# Revit family: Reece_Basin_Alape_Scopio_Freestanding Basin_400 mm
name_source: partatom
category: Plumbing Fixtures
revit_build: Autodesk Revit 2018 (Build: 20180329_1100(x64)
units: mm (PartAtom-declared; Revit-internal decimal feet)

## family parameters
Always vertical = Yes
Cut with Voids When Loaded = Yes
Part Type = Normal
Room Calculation Point = Yes
Round Connector Dimension = Use Diameter
Shared = Yes
Work Plane-Based = Yes

## types (1)
- 8.7 L_Enamelled Glazed Steel_White
    Default Elevation = 0 mm  [stored 0 ft]
    Description = Alape Scopio Freestanding Basin 400mm White
    Disclaimer = THIS FILE IS THE PROPERTY OF THE REECE GROUP. IT MAY NOT BE REPRODUCED, REVERSE-ENGINEERED OR MODIFIED. ANY REPUBLICATION, TRANSMISSION OR DISTRIBUTION FOR THE PURPOSE OF COMMERCIALLY EXPLOITING THE FILES IS PROHIBITED.
    Keynote = Product #9508138, Reece_Basin_Alape_Scopio_Freestanding Basin_400 mm - 8.7 L_Enamelled Glazed Steel_White
    Manufacturer = Alape
    Model = Scopio
    Reece_Basin_Outlet = 32 mm  [stored 0.104987 ft]
    Reece_Detail_Additional = With Wall Connection
    Reece_Detail_Connector = No Taphole
    Reece_Detail_Disclaimer = THIS FILE IS THE PROPERTY OF THE REECE GROUP. IT MAY NOT BE REPRODUCED, REVERSE-ENGINEERED OR MODIFIED. ANY REPUBLICATION, TRANSMISSION OR DISTRIBUTION FOR THE PURPOSE OF COMMERCIALLY EXPLOITING THE FILES IS PROHIBITED.
    Reece_Detail_Installation = Freestanding Basin
    Reece_Material_Main = Reece_Metal_Steel Enamelled_White
    Reece_Overall_Capacity = 8.7 L
    Reece_Overall_Height = 900 mm  [stored 2.95276 ft]
    Reece_Overall_Length = 425 mm  [stored 1.39436 ft]
    Reece_Overall_Width = 400 mm  [stored 1.31234 ft]
    Reece_Product_Brand = Alape
    Reece_Product_Description = Alape Scopio Freestanding Basin 400mm White (Wall Attached)
    Reece_Product_Mount = Wall Mounted
    Reece_Product_Number = 9508138
    Reece_Product_Sub Brand = Scopio
    Reece_Product_Type = Basin
    Reece_Product_Web Page = https://www.reece.com.au
    Type Comments = Basin
    URL = https://www.reece.com.au

note: [stored X ft] marks values corroborated as IEEE doubles in the binary element streams (Revit-internal decimal feet)

## geometry (parser evidence)
native form markers: Sweep x2
no freeform markers — native parametric forms only
